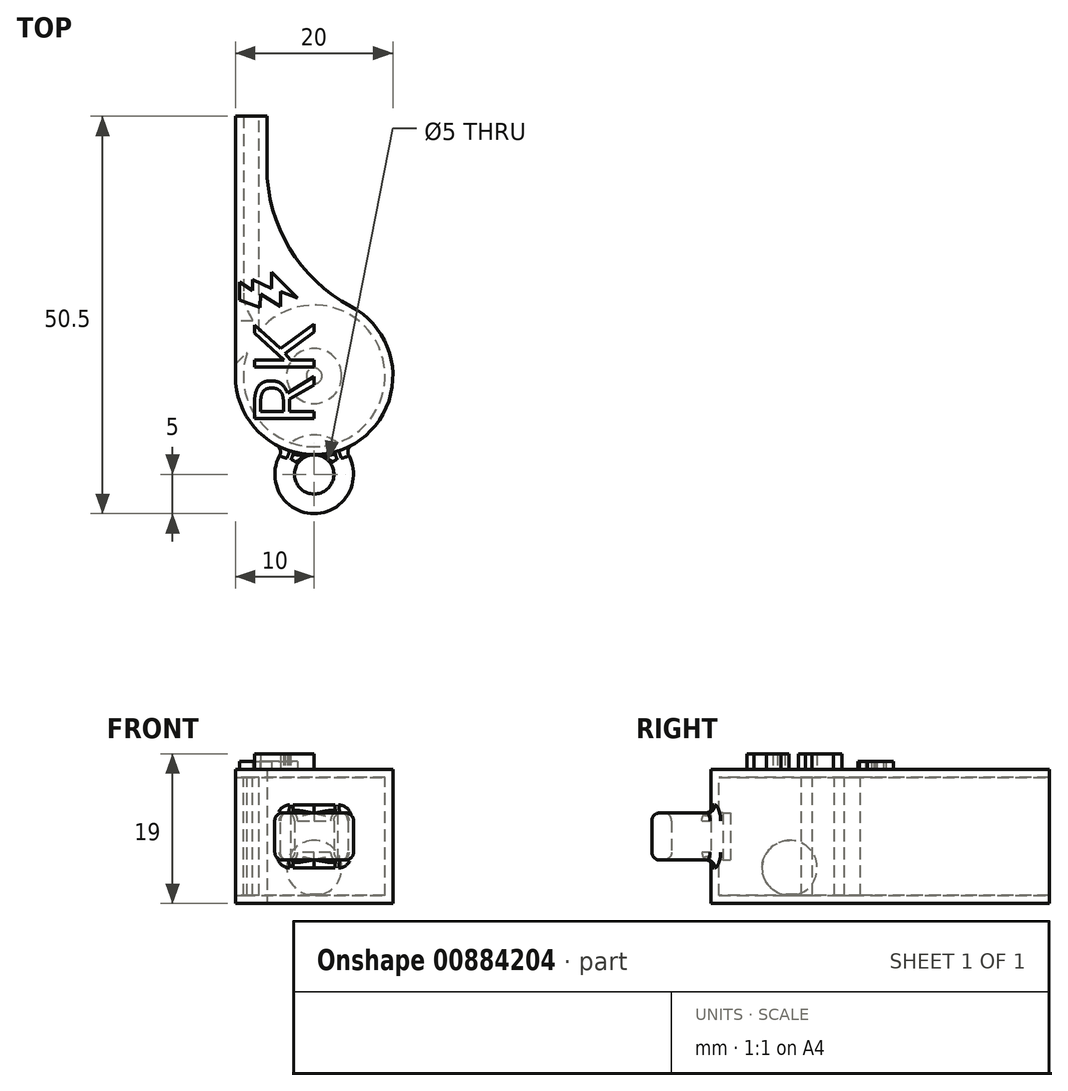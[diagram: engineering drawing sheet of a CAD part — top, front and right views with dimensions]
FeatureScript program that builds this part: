
annotation { "Feature Type Name" : "Feature", "Feature Type Description" : "" }
export const myFeature = defineFeature(function(context is Context, id is Id, definition is map)
    precondition{}
    {
        {
            var Q0;
            Q0=qCreatedBy(makeId("Top.planeOp"),FACE);
            var sketch = newSketch(context, id + "F0", { "sketchPlane" : qUnion([Q0])});
            skArc(sketch, "E0.0.4", {"start": v(-10, 0) * mm, "mid": v(5.16, -8.56) * mm, "end": v(4.67, 8.84) * mm});
            skLineSegment(sketch, "E0.0.3", {"start": v(-10, 33) * mm, "end": v(-10, 0) * mm});
            skLineSegment(sketch, "E0.0.2", {"start": v(-6, 33) * mm, "end": v(-10, 33) * mm});
            skLineSegment(sketch, "E0.0.1", {"start": v(-6, 26.53) * mm, "end": v(-6, 33) * mm});
            skArc(sketch, "E0.0.0", {"start": v(4.67, 8.84) * mm, "mid": v(-3.13, 16.2) * mm, "end": v(-6, 26.53) * mm});
            skSolve(sketch);
        }
        {
            var Q0;
            Q0=makeQuery(id+"F0.imprint","IMPRINT",FACE,{"disambiguationData":[TD([[makeQuery(id+"F0.imprint","IMPRINT",EDGE,{"derivedFrom":sQuery(id+"F0.wireOp",EDGE,"E0.0.4")}),1.0]])]});
            extrude(context, id + "F1", {"entities" : qUnion([Q0]), "endBound" : BoundingType.SYMMETRIC, "depth" : 17 * mm});
        }
        {
            var Q0;
            Q0=qCreatedBy(makeId("Top.planeOp"),FACE);
            var sketch = newSketch(context, id + "F2", { "sketchPlane" : qUnion([Q0])});
            skLineSegment(sketch, "E1.0", {"start": v(-9, 33) * mm, "end": v(-9, 10.5) * mm});
            skLineSegment(sketch, "E2.0", {"start": v(-7, 5.66) * mm, "end": v(-7, 33) * mm});
            skArc(sketch, "E3.0", {"start": v(-8.53, 2.87) * mm, "mid": v(7.89, -4.33) * mm, "end": v(-7, 5.66) * mm});
            skLineSegment(sketch, "E4.0", {"start": v(-10, 1.48) * mm, "end": v(-8.58, 2.9) * mm});
            skArc(sketch, "E5.0", {"start": v(-8.03, 7.54) * mm, "mid": v(-8.75, 8.94) * mm, "end": v(-9, 10.5) * mm});
            skArc(sketch, "E6.0", {"start": v(-7.8, 6.95) * mm, "mid": v(-7.87, 7.26) * mm, "end": v(-8.03, 7.54) * mm});
            skLineSegment(sketch, "E7.0", {"start": v(-7.8, 6.95) * mm, "end": v(-10, 6.95) * mm});
            skLineSegment(sketch, "E8", {"start": v(-7, 33) * mm, "end": v(-9, 33) * mm});
            skLineSegment(sketch, "E9", {"start": v(-10, 6.95) * mm, "end": v(-10, 1.48) * mm});
            skPoint(sketch, "E10.visualSharp", {"position": v(-8.49, 3) * mm});
            skArc(sketch, "E10.filletArc", {"start": v(-8.53, 2.87) * mm, "mid": v(-8.54, 2.9) * mm, "end": v(-8.58, 2.9) * mm});
            skSolve(sketch);
        }
        {
            var Q0;
            Q0=makeQuery(id+"F2.imprint","IMPRINT",FACE,{"disambiguationData":[TD([[makeQuery(id+"F2.imprint","IMPRINT",EDGE,{"derivedFrom":sQuery(id+"F2.wireOp",EDGE,"E1.0")}),1.0]])]});
            extrude(context, id + "F3", {"entities" : qUnion([Q0]), "operationType" : NewBodyOperationType.REMOVE, "endBound" : BoundingType.SYMMETRIC, "oppositeDirection" : true, "depth" : 15 * mm});
        }
        {
            var Q0;
            Q0=qCreatedBy(makeId("Right.planeOp"),FACE);
            var sketch = newSketch(context, id + "F4", { "sketchPlane" : qUnion([Q0])});
            skArc(sketch, "E11", {"start": v(0, -7.5) * mm, "mid": v(3.5, -4) * mm, "end": v(0, -0.5) * mm});
            skLineSegment(sketch, "E12.0", {"start": v(-9, -7.5) * mm, "end": v(9, -7.5) * mm, "construction": true});
            skLineSegment(sketch, "E13", {"start": v(0, 3.94) * mm, "end": v(0, -16.8) * mm, "construction": true});
            skLineSegment(sketch, "E14", {"start": v(0, -7.5) * mm, "end": v(0, -0.5) * mm});
            skSolve(sketch);
        }
        {
            var Q0;
            Q0=makeQuery(id+"F4.imprint","IMPRINT",FACE,{"disambiguationData":[TD([[makeQuery(id+"F4.imprint","IMPRINT",EDGE,{"derivedFrom":sQuery(id+"F4.wireOp",EDGE,"E11")}),1.0]])]});
            var Q1;
            Q1=sQuery(id+"F4.wireOp",EDGE,"E11");
            var Q2;
            Q2=sQuery(id+"F4.wireOp",EDGE,"E13");
            revolve(context, id + "F5", {"entities" : qUnion([Q0]), "surfaceEntities" : qUnion([Q1]), "axis" : qUnion([Q2]), "revolveType" : RevolveType.FULL});
        }
        {
            var Q0;
            Q0=qCreatedBy(makeId("Top.planeOp"),FACE);
            var sketch = newSketch(context, id + "F6", { "sketchPlane" : qUnion([Q0])});
            skArc(sketch, "E15", {"start": v(-3.8, -9.25) * mm, "mid": v(0, -17.5) * mm, "end": v(3.8, -9.25) * mm});
            skCircle(sketch, "E16", {"center": v(0, -12.5) * mm, "radius": 2.5 * mm});
            skPoint(sketch, "E17.orphan", {"position": v(-10, 0) * mm});
            skPoint(sketch, "E18.orphan", {"position": v(4.67, 8.84) * mm});
            skArc(sketch, "E19", {"start": v(-3.8, -9.25) * mm, "mid": v(0, -7.5) * mm, "end": v(3.8, -9.25) * mm});
            skSolve(sketch);
        }
        {
            var Q0;
            {var subQ1=sQuery(id+"F6.wireOp",EDGE,"E15");Q0=makeQuery(id+"F6.imprint","IMPRINT",FACE,{"disambiguationData":[TD([[makeQuery(id+"F6.imprint","IMPRINT",EDGE,{"derivedFrom":subQ1}),1.0]])]});}
            extrude(context, id + "F7", {"entities" : qUnion([Q0]), "operationType" : NewBodyOperationType.ADD, "endBound" : BoundingType.SYMMETRIC, "depth" : 6 * mm});
        }
        {
            var Q0;
            {var subQ0=sQuery(id+"F6.wireOp",EDGE,"E15");var subQ1=sQuery(id+"F6.wireOp",EDGE,"E19");Q0=makeQuery(id+"F7.boolean.opBoolean","SPLIT",FACE,{"disambiguationData":[TD([makeQuery(id+"F1.opExtrude","SWEPT_FACE",FACE,{"disambiguationData":[OSD([sQuery(id+"F0.wireOp",EDGE,"E0.0.4")])]})])],"derivedFrom":makeQuery(id+"F7.opExtrude","SWEPT_FACE",FACE,{"disambiguationData":[OSD([subQ0,subQ1])]})});}
            var Q1;
            {var subQ0=sQuery(id+"F6.wireOp",EDGE,"E15");var subQ1=sQuery(id+"F6.wireOp",EDGE,"E16");var subQ2=sQuery(id+"F6.wireOp",EDGE,"E19");Q1=makeQuery(id+"F7.boolean.opBoolean","SPLIT",FACE,{"disambiguationData":[TD([makeQuery(id+"F1.opExtrude","SWEPT_FACE",FACE,{"disambiguationData":[OSD([sQuery(id+"F0.wireOp",EDGE,"E0.0.4")])]})])],"derivedFrom":makeQuery(id+"F7.opExtrude","CAP_FACE",FACE,{"disambiguationData":[OSD([subQ0,subQ1,subQ2])],"isStart":false})});}
            var Q2;
            {var subQ0=sQuery(id+"F6.wireOp",EDGE,"E15");var subQ1=sQuery(id+"F6.wireOp",EDGE,"E16");var subQ2=sQuery(id+"F6.wireOp",EDGE,"E19");Q2=makeQuery(id+"F7.boolean.opBoolean","SPLIT",FACE,{"disambiguationData":[TD([makeQuery(id+"F1.opExtrude","SWEPT_FACE",FACE,{"disambiguationData":[OSD([sQuery(id+"F0.wireOp",EDGE,"E0.0.4")])]})])],"derivedFrom":makeQuery(id+"F7.opExtrude","CAP_FACE",FACE,{"disambiguationData":[OSD([subQ0,subQ1,subQ2])],"isStart":true})});}
            var Q3;
            Q3=makeQuery(id+"F3.boolean.opBoolean","COPY",EDGE,{"derivedFrom":makeQuery(id+"F3.opExtrude","CAP_EDGE",EDGE,{"disambiguationData":[OSD([sQuery(id+"F2.wireOp",EDGE,"E8")])],"isStart":true})});
            var Q4;
            Q4=makeQuery(id+"F3.boolean.opBoolean","COPY",EDGE,{"derivedFrom":makeQuery(id+"F3.opExtrude","SWEPT_EDGE",EDGE,{"disambiguationData":[OSD([sQuery(id+"F2.wireOp",EDGE,"E1.0"),sQuery(id+"F2.wireOp",EDGE,"E8")])]})});
            var Q5;
            Q5=makeQuery(id+"F3.boolean.opBoolean","COPY",EDGE,{"derivedFrom":makeQuery(id+"F3.opExtrude","SWEPT_EDGE",EDGE,{"disambiguationData":[OSD([sQuery(id+"F2.wireOp",EDGE,"E2.0"),sQuery(id+"F2.wireOp",EDGE,"E8")])]})});
            var Q6;
            Q6=makeQuery(id+"F3.boolean.opBoolean","COPY",EDGE,{"derivedFrom":makeQuery(id+"F3.opExtrude","CAP_EDGE",EDGE,{"disambiguationData":[OSD([sQuery(id+"F2.wireOp",EDGE,"E8")])],"isStart":false})});
            fillet(context, id + "F8", {"entities" : qUnion([Q0, Q1, Q2, Q3, Q4, Q5, Q6]), "radius" : 1 * mm, "tangentPropagation" : true, "allowEdgeOverflow" : false});
        }
        {
            var Q0;
            Q0=makeQuery(id+"F1.opExtrude","CAP_FACE",FACE,{"disambiguationData":[OSD([sQuery(id+"F0.wireOp",EDGE,"E0.0.4"),sQuery(id+"F0.wireOp",EDGE,"E0.0.3"),sQuery(id+"F0.wireOp",EDGE,"E0.0.2"),sQuery(id+"F0.wireOp",EDGE,"E0.0.1"),sQuery(id+"F0.wireOp",EDGE,"E0.0.0")])],"isStart":false});
            var sketch = newSketch(context, id + "F9", { "sketchPlane" : qUnion([Q0])});
            skText(sketch, "E20", { "text": "RK", "fontName": "OpenSans-Regular.ttf"});
            const initialGuessF9  = {"E20": [0, -0.00646, 0, 1, 0.00764]};
            skSetInitialGuess(sketch, initialGuessF9);
            skSolve(sketch);
        }
        {
            var Q0;
            Q0=makeQuery(id+"F3.boolean.opBoolean","COPY",FACE,{"derivedFrom":makeQuery(id+"F3.opExtrude","CAP_FACE",FACE,{"disambiguationData":[OSD([sQuery(id+"F2.wireOp",EDGE,"E1.0"),sQuery(id+"F2.wireOp",EDGE,"E2.0"),sQuery(id+"F2.wireOp",EDGE,"E3.0"),sQuery(id+"F2.wireOp",EDGE,"E4.0"),sQuery(id+"F2.wireOp",EDGE,"E5.0"),sQuery(id+"F2.wireOp",EDGE,"E6.0"),sQuery(id+"F2.wireOp",EDGE,"E7.0"),sQuery(id+"F2.wireOp",EDGE,"E8"),sQuery(id+"F2.wireOp",EDGE,"E9"),sQuery(id+"F2.wireOp",EDGE,"E10.filletArc")])],"isStart":false})});
            var sketch = newSketch(context, id + "F10", { "sketchPlane" : qUnion([Q0])});
            skCircle(sketch, "E21", {"center": v(0, 0) * mm, "radius": 1 * mm});
            skSolve(sketch);
        }
        {
            var Q0;
            Q0=qSketchRegion(id+"F10",true);
            extrude(context, id + "F11", {"entities" : qUnion([Q0]), "operationType" : NewBodyOperationType.ADD, "depth" : 2 * mm});
        }
        {
            var Q0;
            Q0=qSketchRegion(id+"F9",true);
            extrude(context, id + "F12", {"entities" : qUnion([Q0]), "operationType" : NewBodyOperationType.ADD, "offsetDistance" : 25 * mm, "depth" : 2 * mm});
        }
        {
            var Q0;
            {var subQ1=sQuery(id+"F0.wireOp",EDGE,"E0.0.4");var subQ2=sQuery(id+"F0.wireOp",EDGE,"E0.0.0");var subQ3=sQuery(id+"F0.wireOp",EDGE,"E0.0.3");var subQ4=sQuery(id+"F0.wireOp",EDGE,"E0.0.1");Q0=makeQuery(id+"F12.boolean.opBoolean","SPLIT",FACE,{"disambiguationData":[TD([makeQuery(id+"F1.opExtrude","SWEPT_FACE",FACE,{"disambiguationData":[OSD([subQ1])]})])],"derivedFrom":makeQuery(id+"F1.opExtrude","CAP_FACE",FACE,{"disambiguationData":[OSD([subQ1,subQ3,sQuery(id+"F0.wireOp",EDGE,"E0.0.2"),subQ4,subQ2])],"isStart":false})});}
            var sketch = newSketch(context, id + "F13", { "sketchPlane" : qUnion([Q0])});
            skLineSegment(sketch, "E22", {"start": v(-6.87, 8.68) * mm, "end": v(-6.8, 10.39) * mm});
            skLineSegment(sketch, "E23", {"start": v(-6.8, 10.39) * mm, "end": v(-4.25, 8.84) * mm});
            skLineSegment(sketch, "E24", {"start": v(-4.25, 10.7) * mm, "end": v(-2.14, 9.9) * mm});
            skLineSegment(sketch, "E25", {"start": v(-2.14, 9.9) * mm, "end": v(-5.44, 13.2) * mm});
            skLineSegment(sketch, "E26", {"start": v(-5.44, 13.2) * mm, "end": v(-5.44, 11.1) * mm});
            skLineSegment(sketch, "E27", {"start": v(-5.44, 11.1) * mm, "end": v(-7.8, 12.22) * mm});
            skLineSegment(sketch, "E28", {"start": v(-7.8, 12.22) * mm, "end": v(-7.8, 10.85) * mm});
            skLineSegment(sketch, "E29", {"start": v(-4.25, 8.84) * mm, "end": v(-4.25, 10.7) * mm});
            skPoint(sketch, "E30.orphan", {"position": v(-9.45, 8.84) * mm});
            skPoint(sketch, "E31.start.orphan", {"position": v(-8.25, 8.84) * mm});
            skLineSegment(sketch, "E32", {"start": v(-9.46, 11.91) * mm, "end": v(-7.8, 10.85) * mm});
            skLineSegment(sketch, "E33", {"start": v(-9.46, 9.62) * mm, "end": v(-9.46, 11.91) * mm});
            skLineSegment(sketch, "E34", {"start": v(-9.46, 9.62) * mm, "end": v(-6.87, 8.68) * mm});
            skSolve(sketch);
        }
        {
            var Q0;
            Q0=makeQuery(id+"F13.imprint","IMPRINT",FACE,{"disambiguationData":[TD([[makeQuery(id+"F13.imprint","IMPRINT",EDGE,{"derivedFrom":sQuery(id+"F13.wireOp",EDGE,"E22")}),1.0]])]});
            extrude(context, id + "F14", {"entities" : qUnion([Q0]), "operationType" : NewBodyOperationType.ADD, "depth" : 1 * mm});
        }
    });
